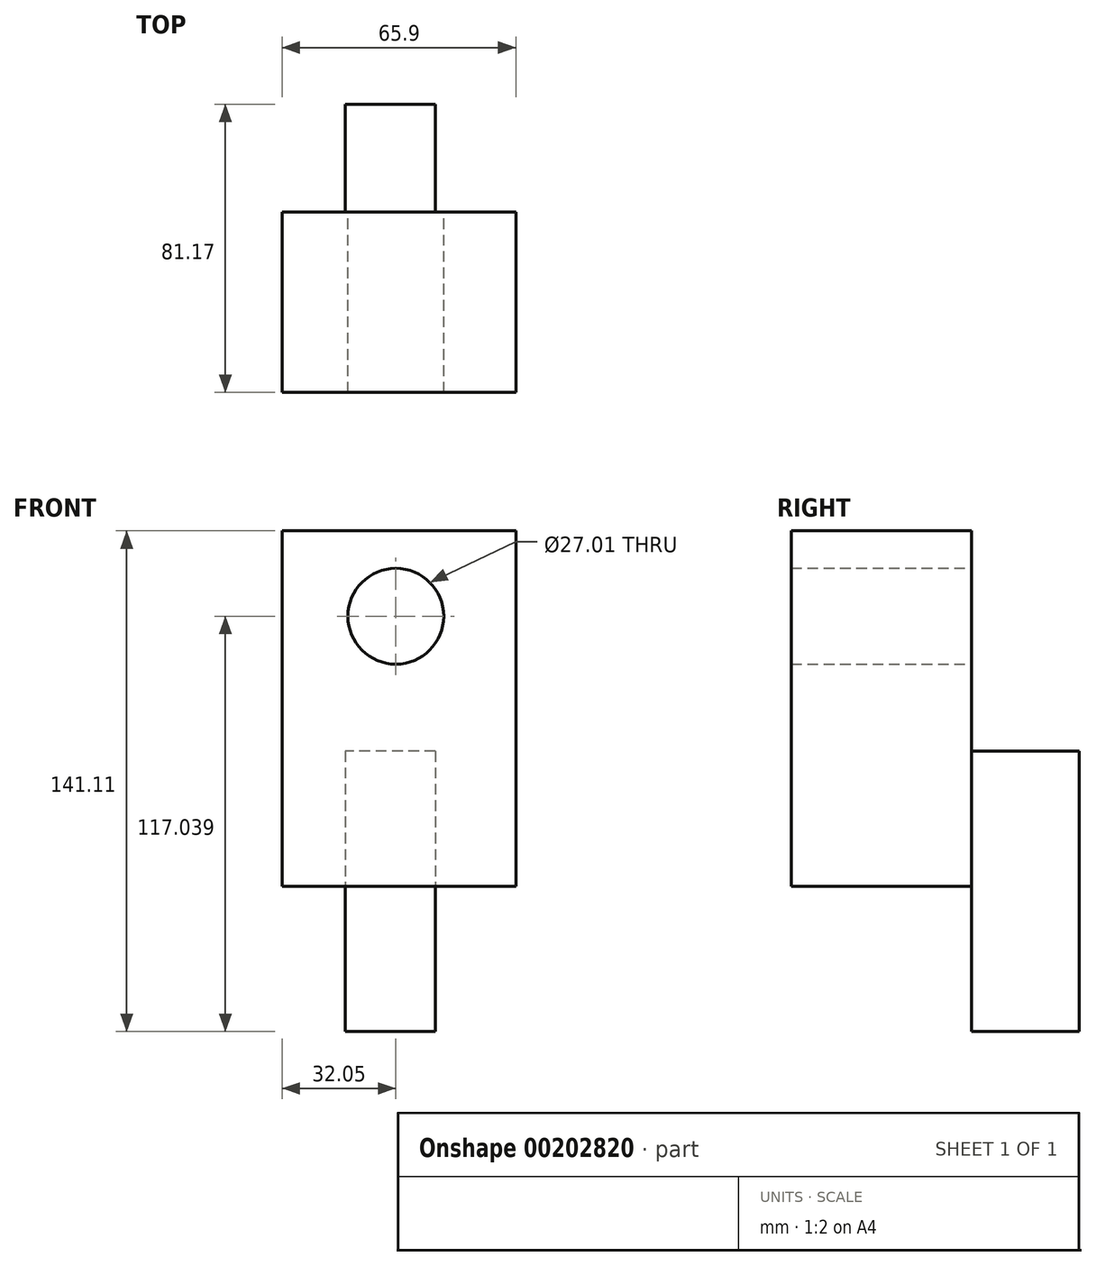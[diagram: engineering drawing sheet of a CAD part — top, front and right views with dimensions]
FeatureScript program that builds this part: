
annotation { "Feature Type Name" : "Feature", "Feature Type Description" : "" }
export const myFeature = defineFeature(function(context is Context, id is Id, definition is map)
    precondition{}
    {
        {
            var Q0;
            Q0=qCreatedBy(makeId("Front.planeOp"),FACE);
            var sketch = newSketch(context, id + "F0", { "sketchPlane" : qUnion([Q0])});
            skLineSegment(sketch, "E0.bottom", {"start": v(48.12, 62.1) * mm, "end": v(-17.78, 62.1) * mm});
            skLineSegment(sketch, "E0.top", {"start": v(48.12, -38.05) * mm, "end": v(-17.78, -38.05) * mm});
            skLineSegment(sketch, "E0.left", {"start": v(48.12, 62.1) * mm, "end": v(48.12, -38.05) * mm});
            skLineSegment(sketch, "E0.right", {"start": v(-17.78, 62.1) * mm, "end": v(-17.78, -38.05) * mm});
            skPoint(sketch, "E0.middle", {"position": v(15.17, 12.03) * mm});
            skLineSegment(sketch, "E1.bottom", {"start": v(25.18, -38.05) * mm, "end": v(40, -38.05) * mm});
            skLineSegment(sketch, "E1.top", {"start": v(25.18, -57.63) * mm, "end": v(40, -57.63) * mm});
            skLineSegment(sketch, "E1.left", {"start": v(25.18, -38.05) * mm, "end": v(25.18, -57.63) * mm});
            skLineSegment(sketch, "E1.right", {"start": v(40, -38.05) * mm, "end": v(40, -57.63) * mm});
            skCircle(sketch, "E2", {"center": v(14.27, 38.04) * mm, "radius": 13.5 * mm});
            skSolve(sketch);
        }
        {
            var Q0;
            Q0=makeQuery(id+"F0.imprint","IMPRINT",FACE,{"disambiguationData":[TD([[makeQuery(id+"F0.imprint","IMPRINT",EDGE,{"derivedFrom":sQuery(id+"F0.wireOp",EDGE,"E0.bottom")}),1.0]])]});
            var Q1;
            Q1=makeQuery(id+"F0.imprint","IMPRINT",FACE,{"disambiguationData":[TD([[makeQuery(id+"F0.imprint","IMPRINT",EDGE,{"derivedFrom":sQuery(id+"F0.wireOp",EDGE,"E1.bottom")}),-1.0]])]});
            extrude(context, id + "F1", {"entities" : qUnion([Q0, Q1]), "depth" : 25.4 * mm});
        }
        {
            var Q0;
            Q0=makeQuery(id+"F1.opExtrude","CAP_FACE",FACE,{"disambiguationData":[OSD([sQuery(id+"F0.wireOp",EDGE,"E0.bottom"),sQuery(id+"F0.wireOp",EDGE,"E0.top"),sQuery(id+"F0.wireOp",EDGE,"E0.left"),sQuery(id+"F0.wireOp",EDGE,"E0.right"),sQuery(id+"F0.wireOp",EDGE,"E1.top"),sQuery(id+"F0.wireOp",EDGE,"E1.left"),sQuery(id+"F0.wireOp",EDGE,"E1.right"),sQuery(id+"F0.wireOp",EDGE,"E2")])],"isStart":false});
            extrude(context, id + "F2", {"entities" : qUnion([Q0]), "operationType" : NewBodyOperationType.ADD, "depth" : 25.4 * mm});
        }
        {
            var Q0;
            Q0=qCreatedBy(makeId("Right.planeOp"),FACE);
            var sketch = newSketch(context, id + "F3", { "sketchPlane" : qUnion([Q0])});
            skLineSegment(sketch, "E3.bottom", {"start": v(0, -79) * mm, "end": v(30.37, -79) * mm});
            skLineSegment(sketch, "E3.top", {"start": v(0, 0) * mm, "end": v(30.37, 0) * mm});
            skLineSegment(sketch, "E3.left", {"start": v(0, 0) * mm, "end": v(0, -79) * mm});
            skLineSegment(sketch, "E3.right", {"start": v(30.37, 0) * mm, "end": v(30.37, -79) * mm});
            skSolve(sketch);
        }
        {
            var Q0;
            Q0 = qSketchRegion(id + "F3", true);
            extrude(context, id + "F4", {"entities" : qUnion([Q0]), "operationType" : NewBodyOperationType.ADD, "depth" : 25.4 * mm});
        }
    });
